# Revit family: FU_Modular_Sandler_Ari 1313
name_source: partatom
category: Furniture
units: mm (PartAtom-declared; Revit-internal decimal feet)

## family parameters
Always vertical = Yes
Cut with Voids When Loaded = No
OmniClass Number = 23.40.20.00
OmniClass Title = General Furniture and Specialties
Room Calculation Point = No
Shared = No
Work Plane-Based = No

## types (1)
- Ari 1313
    Default Elevation = 0 mm  [stored 0 ft]
    Depth = 710 mm  [stored 2.3294 ft]
    Description = Upholstered indoor element that can be used as a backless sofa seat or a freestanding square ottoman. Part of the Ari indoor modular seating range.
    Height = 780 mm  [stored 2.55906 ft]
    Manufacturer = Sandler
    Model = Ari 1313
    URL = https://www.sandlerseating.com
    Width = 710 mm  [stored 2.3294 ft]

note: [stored X ft] marks values corroborated as IEEE doubles in the binary element streams (Revit-internal decimal feet)

## geometry (parser evidence)
native form markers: Sweep x3
no freeform markers — native parametric forms only
